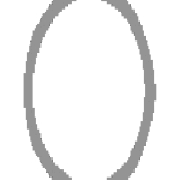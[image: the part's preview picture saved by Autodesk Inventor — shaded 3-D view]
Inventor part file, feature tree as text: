
AUTODESK INVENTOR PART (.ipt)
format: ipt  version: 2021 (Build 250183000, 183)  size: 113,152 bytes
history: native  units: in
note: dims shown in document units (in); Inventor stores cm internally (conversion verified against a paired STEP export)
features: other x4, sketch x3, plane x1
ambient origin geometry x8: Origin, YZ Plane, XZ Plane, XY Plane, X Axis, Y Axis, Z Axis, Center Point
bodies: Solid1 (feature_tree), Body (feature_tree)
feature tree (8):
  other  "Driven Length"
  other  "Frame Generator"
  other  "Start Plane"
  other  "End Plane"
  sketch  "Sketch"  dims[d2=21.5in d4=-0.0in d5=21.5in d6=0.12in d7=0.0in d8=90.0deg d9=21.5in]
  sketch  "Sketch2"  dims[d0=1.0in]
  plane  "Work Plane3"
  sketch  "Sketch3"  dims[d1=0.065in]
